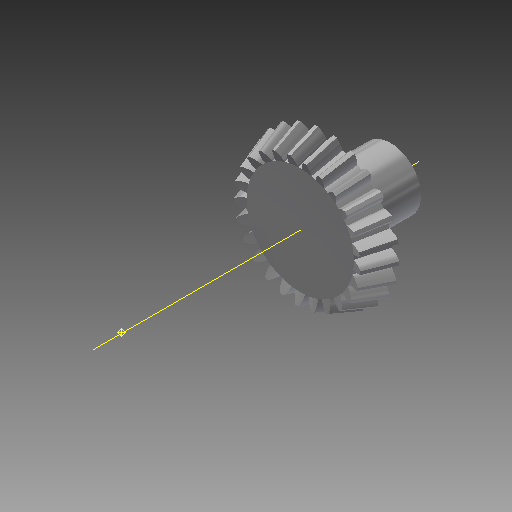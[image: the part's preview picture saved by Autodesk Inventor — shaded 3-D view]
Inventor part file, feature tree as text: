
AUTODESK INVENTOR PART (.ipt)
format: ipt  version: 2019 (Build 230136000, 136)  size: 640,000 bytes
history: native  units: mm
features: other x24, sketch x3, loft x2, pattern_circular x2, extrude x2
ambient origin geometry x6: Origin, XZ Plane, X Axis, Y Axis, Z Axis, Center Point
bodies: Solid1 (feature_tree)
feature tree (33):
  other  "Top Point"
  other  "Mesh Plane2"
  other  "Teeth Body"
  other  "Start Point"
  other  "Tooth Plane"
  other  "Start Sketch"
  other  "End Point"
  other  "3D Sketch Right"
  other  "End Plane Right"
  loft  "Loft Right"
  pattern_circular  "Circular Pattern Right"  Count=5  [1 undecoded]
  other  "3D Sketch Left"
  other  "End Plane Left"
  loft  "Loft Left"
  pattern_circular  "Circular Pattern Left"  [2 undecoded]
  other  "Fix Body"
  extrude  "Extrusion1"  Depth=70.0mm
  extrude  "Extrusion2"  Depth=70.0mm
  other  "Mesh Plane"
  other  "Top Plane"
  other  "Teeth Body Sketch"
  other  "End Plane"
  other  "End Sketch"
  other  "Helical Curve Left"
  other  "End Sketch Left"
  other  "Body Sketch"
  sketch  "Sketch6"  dims[d0=225.0mm d1=204.508441mm]
  other  "Srf1"
  other  "Helical Curve Right"
  other  "End Sketch Right"
  sketch  "Sketch8"  dims[d2=242.076299mm d3=50.0mm]
  sketch  "Sketch9"  dims[d4=334.65395mm d5=90.0deg d7=43.615489mm d8=47.040386mm d9=100.74928mm d11=50.99mm d12=37.407763mm d15=40.3452mm d16=86.409788mm d17=0.0mm d18=90.0deg d19=0.0mm d20=90.0deg d21=250.0mm d22=360.0deg d26=1712.944518mm d27=48.373361mm d28=225.0mm d29=-3.217506mm d30=37.407763mm d31=40.3452mm d32=86.409788mm d35=0.0mm d37=0.0mm d39=0.0mm d40=90.0deg d41=250.0mm d42=360.0deg d46=90.0deg d47=90.0deg d48=0.0mm d49=0.0mm d50=90.0deg d51=1.256637mm d52=0.0mm d53=0.0mm d54=0.0mm d56=98.688887mm d57=133.525412mm d58=105.409412mm d59=114.520944mm d60=90.406651mm d61=114.520944mm d62=90.406651mm d65=1712.944518mm d66=31.5mm d67=225.0mm d68=-3.217506mm d69=48.373361mm d70=40.3452mm d71=86.409788mm d72=37.407763mm d73=90.406651mm d74=114.520944mm d75=0.0mm d77=0.0mm d79=0.0mm d80=90.0deg d81=250.0mm d82=360.0deg d84=10.0mm d85=20.0mm d86=20.0mm d87=10.0mm d88=0.0mm d89=0.0mm d90=90.0deg d91=90.0deg d92=90.0deg d93=90.0deg d94=100.0mm d97=100.0mm d98=0.0mm d99=38.0mm d100=70.0mm d101=0.0mm]
  other  "Pitch Diameter"
note: 3 required parameter values undecoded (feature->parameter linkage not recoverable at this tier; creation-order binding heuristic only, values carry confidence <= 0.55)
